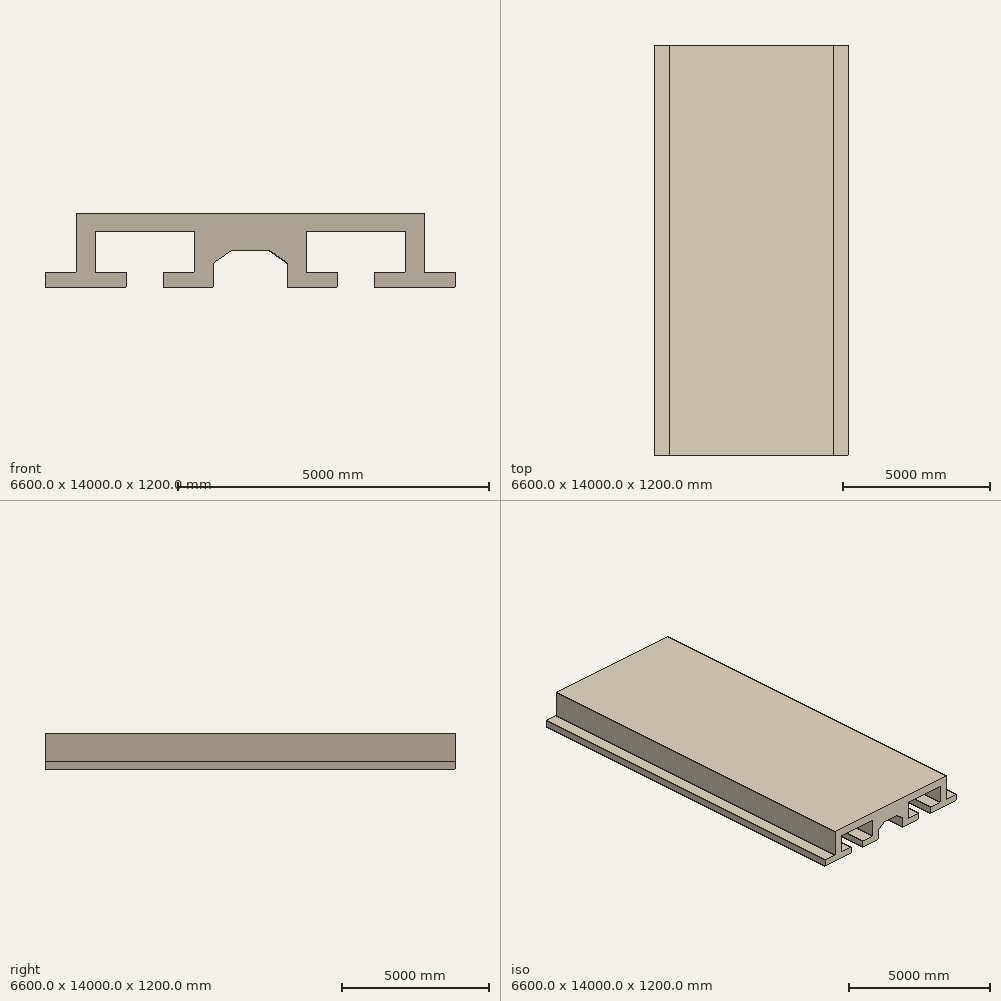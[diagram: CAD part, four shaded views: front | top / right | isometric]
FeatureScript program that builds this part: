
annotation { "Feature Type Name" : "Feature", "Feature Type Description" : "" }
export const myFeature = defineFeature(function(context is Context, id is Id, definition is map)
    precondition{}
    {
        {
            var Q0;
            Q0=qCreatedBy(makeId("Front.planeOp"),FACE);
            var sketch = newSketch(context, id + "F0", { "sketchPlane" : qUnion([Q0])});
            skLineSegment(sketch, "E0", {"start": v(-400, 1050) * mm, "end": v(-400, 1700) * mm});
            skLineSegment(sketch, "E1", {"start": v(-400, 1700) * mm, "end": v(1200, 1700) * mm});
            skLineSegment(sketch, "E2", {"start": v(1200, 1700) * mm, "end": v(1200, 1050) * mm});
            skLineSegment(sketch, "E3", {"start": v(1200, 1050) * mm, "end": v(700, 1050) * mm});
            skLineSegment(sketch, "E4", {"start": v(700, 1050) * mm, "end": v(700, 800) * mm});
            skLineSegment(sketch, "E5", {"start": v(700, 800) * mm, "end": v(1500, 800) * mm});
            skLineSegment(sketch, "E6", {"start": v(1500, 800) * mm, "end": v(1500, 1189.94) * mm});
            skLineSegment(sketch, "E7", {"start": v(1500, 1189.94) * mm, "end": v(1800, 1400) * mm});
            skLineSegment(sketch, "E8", {"start": v(1800, 1400) * mm, "end": v(2100, 1400) * mm});
            skLineSegment(sketch, "E9", {"start": v(2100, 1400) * mm, "end": v(2100, 2000) * mm});
            skLineSegment(sketch, "E10", {"start": v(2100, 2000) * mm, "end": v(-700, 2000) * mm});
            skLineSegment(sketch, "E11", {"start": v(-700, 2000) * mm, "end": v(-700, 1050) * mm});
            skLineSegment(sketch, "E12", {"start": v(-700, 1050) * mm, "end": v(-1200, 1050) * mm});
            skLineSegment(sketch, "E13", {"start": v(-1200, 1050) * mm, "end": v(-1200, 800) * mm});
            skLineSegment(sketch, "E14", {"start": v(-1200, 800) * mm, "end": v(100, 800) * mm});
            skLineSegment(sketch, "E15", {"start": v(100, 800) * mm, "end": v(100, 1050) * mm});
            skLineSegment(sketch, "E16", {"start": v(100, 1050) * mm, "end": v(-400, 1050) * mm});
            skSolve(sketch);
        }
        {
            var Q0;
            Q0 = qSketchRegion(id + "F0", true);
            extrude(context, id + "F1", {"entities" : qUnion([Q0]), "depth" : 14000 * mm, "offsetDistance" : 25 * mm});
        }
        {
            var Q0;
            Q0=makeQuery(id+"F1.opExtrude","SWEPT_BODY",BODY,{"disambiguationData":[OSD([sQuery(id+"F0.wireOp",EDGE,"E0"),sQuery(id+"F0.wireOp",EDGE,"E1"),sQuery(id+"F0.wireOp",EDGE,"E2"),sQuery(id+"F0.wireOp",EDGE,"E3"),sQuery(id+"F0.wireOp",EDGE,"E4"),sQuery(id+"F0.wireOp",EDGE,"E5"),sQuery(id+"F0.wireOp",EDGE,"E6"),sQuery(id+"F0.wireOp",EDGE,"E7"),sQuery(id+"F0.wireOp",EDGE,"E8"),sQuery(id+"F0.wireOp",EDGE,"E9"),sQuery(id+"F0.wireOp",EDGE,"E10"),sQuery(id+"F0.wireOp",EDGE,"E11"),sQuery(id+"F0.wireOp",EDGE,"E12"),sQuery(id+"F0.wireOp",EDGE,"E13"),sQuery(id+"F0.wireOp",EDGE,"E14"),sQuery(id+"F0.wireOp",EDGE,"E15"),sQuery(id+"F0.wireOp",EDGE,"E16")])]});
            var Q1;
            Q1=makeQuery(id+"F1.opExtrude","SWEPT_FACE",FACE,{"disambiguationData":[OSD([sQuery(id+"F0.wireOp",EDGE,"E9")])]});
            mirror(context, id + "F2", {"operationType" : NewBodyOperationType.ADD, "entities" : qUnion([Q0]), "mirrorPlane" : qUnion([Q1])});
        }
    });
